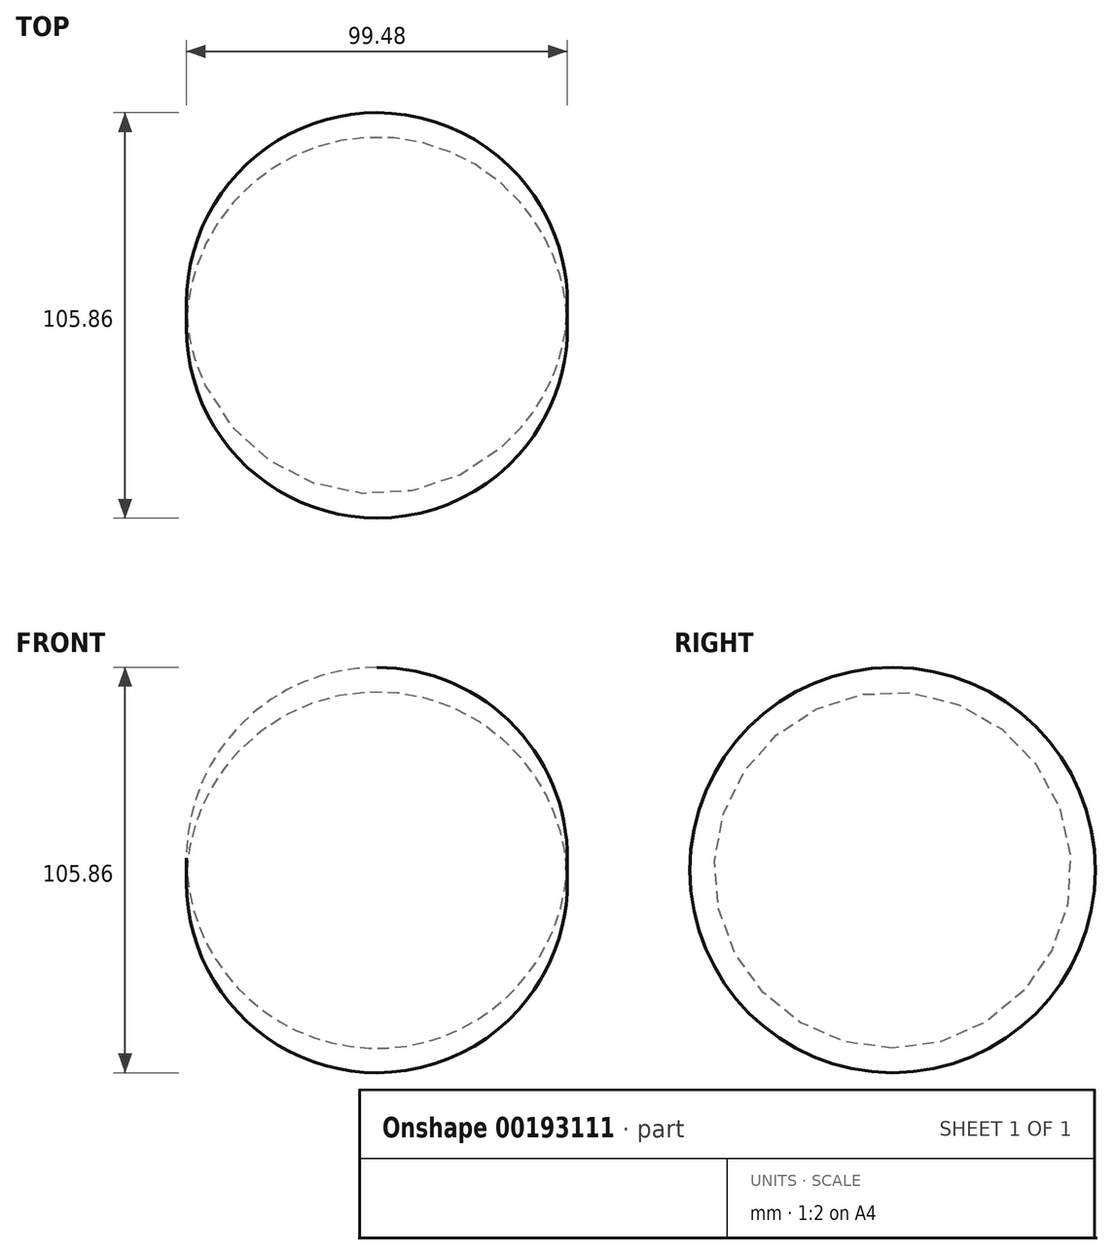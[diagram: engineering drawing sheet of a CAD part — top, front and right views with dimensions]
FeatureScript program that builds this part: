
annotation { "Feature Type Name" : "Feature", "Feature Type Description" : "" }
export const myFeature = defineFeature(function(context is Context, id is Id, definition is map)
    precondition{}
    {
        {
            var Q0;
            Q0=qCreatedBy(makeId("Top.planeOp"),FACE);
            var sketch = newSketch(context, id + "F0", { "sketchPlane" : qUnion([Q0])});
            skArc(sketch, "E0", {"start": v(49.63, -3.2) * mm, "mid": v(0, 49.74) * mm, "end": v(-49.63, -3.2) * mm});
            skLineSegment(sketch, "E1", {"start": v(-49.64, -3.2) * mm, "end": v(49.63, -3.2) * mm});
            skSolve(sketch);
        }
        {
            var Q0;
            Q0 = qSketchRegion(id + "F0", true);
            var Q1;
            Q1=sQuery(id+"F0.wireOp",EDGE,"E1");
            revolve(context, id + "F1", {"entities" : qUnion([Q0]), "axis" : qUnion([Q1]), "revolveType" : RevolveType.FULL});
        }
    });
